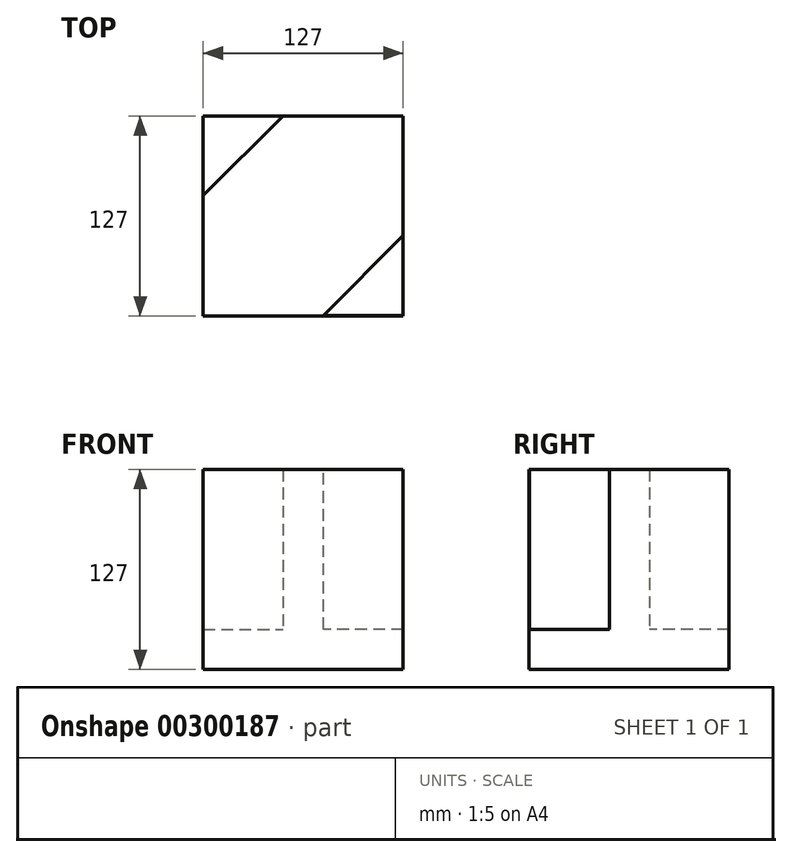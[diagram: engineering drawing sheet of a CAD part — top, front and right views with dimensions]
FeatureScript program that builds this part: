
annotation { "Feature Type Name" : "Feature", "Feature Type Description" : "" }
export const myFeature = defineFeature(function(context is Context, id is Id, definition is map)
    precondition{}
    {
        {
            var Q0;
            Q0=qCreatedBy(makeId("Top.planeOp"),FACE);
            var sketch = newSketch(context, id + "F0", { "sketchPlane" : qUnion([Q0])});
            skLineSegment(sketch, "E0.bottom", {"start": v(63.5, -63.5) * mm, "end": v(-63.5, -63.5) * mm});
            skLineSegment(sketch, "E0.top", {"start": v(63.5, 63.5) * mm, "end": v(-63.5, 63.5) * mm});
            skLineSegment(sketch, "E0.left", {"start": v(63.5, -63.5) * mm, "end": v(63.5, 63.5) * mm});
            skLineSegment(sketch, "E0.right", {"start": v(-63.5, -63.5) * mm, "end": v(-63.5, 63.5) * mm});
            skPoint(sketch, "E0.middle", {"position": v(0, 0) * mm});
            skSolve(sketch);
        }
        {
            var Q0;
            Q0=makeQuery(id+"F0.imprint","IMPRINT",FACE,{"disambiguationData":[TD([[makeQuery(id+"F0.imprint","IMPRINT",EDGE,{"derivedFrom":sQuery(id+"F0.wireOp",EDGE,"E0.bottom")}),-1.0]])]});
            extrude(context, id + "F1", {"entities" : qUnion([Q0]), "oppositeDirection" : true, "depth" : 127 * mm});
        }
        {
            var Q0;
            Q0=qCreatedBy(makeId("Top.planeOp"),FACE);
            var sketch = newSketch(context, id + "F2", { "sketchPlane" : qUnion([Q0])});
            skLineSegment(sketch, "E1", {"start": v(-63.76, 63.52) * mm, "end": v(-63.76, 12.72) * mm});
            skLineSegment(sketch, "E2", {"start": v(-63.76, 63.52) * mm, "end": v(-12.96, 63.52) * mm});
            skLineSegment(sketch, "E3", {"start": v(-63.76, 12.72) * mm, "end": v(-12.96, 63.52) * mm});
            skLineSegment(sketch, "E4", {"start": v(63.54, -63.3) * mm, "end": v(12.74, -63.3) * mm});
            skLineSegment(sketch, "E5", {"start": v(63.54, -63.3) * mm, "end": v(63.54, -12.5) * mm});
            skLineSegment(sketch, "E6", {"start": v(12.74, -63.3) * mm, "end": v(63.54, -12.5) * mm});
            skSolve(sketch);
        }
        {
            var Q0;
            Q0=makeQuery(id+"F2.imprint","IMPRINT",FACE,{"disambiguationData":[TD([[makeQuery(id+"F2.imprint","IMPRINT",EDGE,{"derivedFrom":sQuery(id+"F2.wireOp",EDGE,"E1")}),1.0]])]});
            var Q1;
            Q1=makeQuery(id+"F2.imprint","IMPRINT",FACE,{"disambiguationData":[TD([[makeQuery(id+"F2.imprint","IMPRINT",EDGE,{"derivedFrom":sQuery(id+"F2.wireOp",EDGE,"Dcr9UUed-gmyX-0vqt-4Kux-od7bMp4EwzXa")}),1.0]])]});
            var Q2;
            Q2=makeQuery(id+"F2.imprint","IMPRINT",FACE,{"disambiguationData":[TD([[makeQuery(id+"F2.imprint","IMPRINT",EDGE,{"derivedFrom":sQuery(id+"F2.wireOp",EDGE,"E4")}),-1.0]])]});
            extrude(context, id + "F3", {"entities" : qUnion([Q0, Q1, Q2]), "operationType" : NewBodyOperationType.REMOVE, "oppositeDirection" : true, "depth" : 101.6 * mm});
        }
    });
